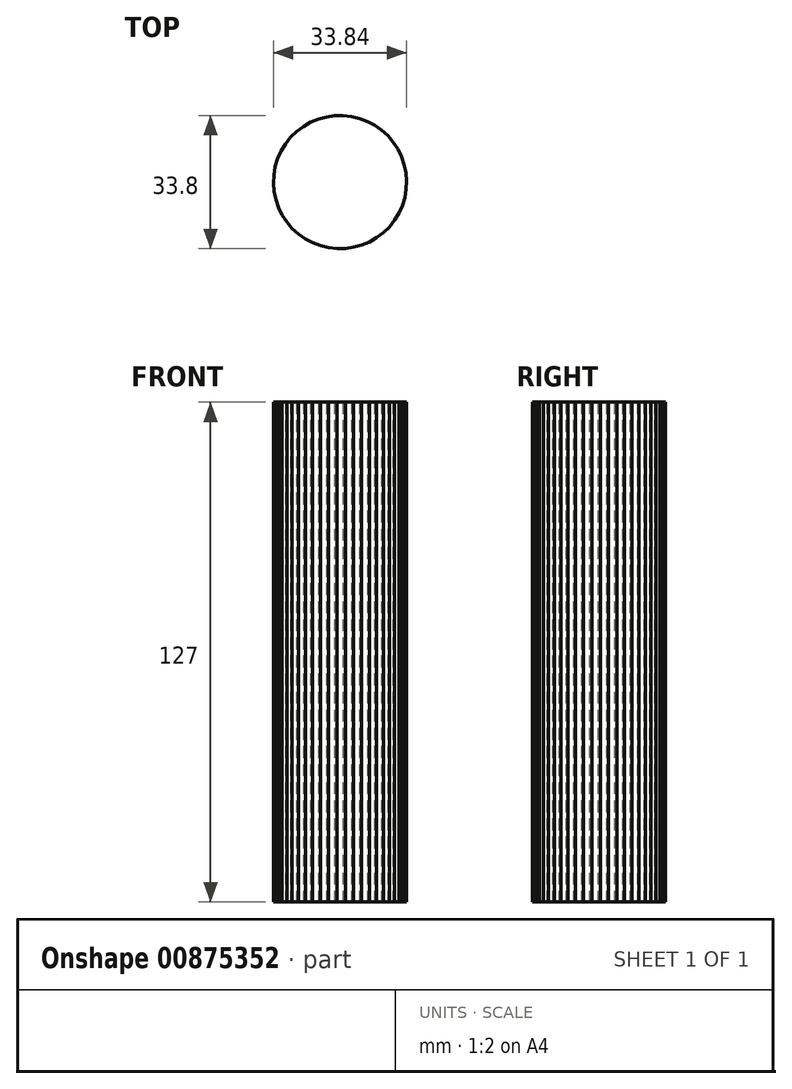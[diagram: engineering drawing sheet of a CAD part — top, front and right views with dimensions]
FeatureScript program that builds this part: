
annotation { "Feature Type Name" : "Feature", "Feature Type Description" : "" }
export const myFeature = defineFeature(function(context is Context, id is Id, definition is map)
    precondition{}
    {
        {
            var Q0;
            Q0=qCreatedBy(makeId("Top.planeOp"),FACE);
            var sketch = newSketch(context, id + "F0", { "sketchPlane" : qUnion([Q0])});
            skCircle(sketch, "E0.cCircle", {"center": v(-26.2, 25.5) * mm, "radius": 16.89 * mm, "construction": true});
            skLineSegment(sketch, "E0.0", {"start": v(-20.7, 9.5) * mm, "end": v(-22.75, 8.93) * mm});
            skLineSegment(sketch, "E0.1", {"start": v(-22.75, 8.93) * mm, "end": v(-24.85, 8.63) * mm});
            skLineSegment(sketch, "E0.2", {"start": v(-24.85, 8.63) * mm, "end": v(-26.97, 8.59) * mm});
            skLineSegment(sketch, "E0.3", {"start": v(-26.97, 8.59) * mm, "end": v(-29.09, 8.82) * mm});
            skLineSegment(sketch, "E0.4", {"start": v(-29.09, 8.82) * mm, "end": v(-31.15, 9.31) * mm});
            skLineSegment(sketch, "E0.5", {"start": v(-31.15, 9.31) * mm, "end": v(-33.14, 10.06) * mm});
            skLineSegment(sketch, "E0.6", {"start": v(-33.14, 10.06) * mm, "end": v(-35.02, 11.05) * mm});
            skLineSegment(sketch, "E0.7", {"start": v(-35.02, 11.05) * mm, "end": v(-36.76, 12.27) * mm});
            skLineSegment(sketch, "E0.8", {"start": v(-36.76, 12.27) * mm, "end": v(-38.33, 13.7) * mm});
            skLineSegment(sketch, "E0.9", {"start": v(-38.33, 13.7) * mm, "end": v(-39.72, 15.31) * mm});
            skLineSegment(sketch, "E0.10", {"start": v(-39.72, 15.31) * mm, "end": v(-40.88, 17.09) * mm});
            skLineSegment(sketch, "E0.11", {"start": v(-40.88, 17.09) * mm, "end": v(-41.82, 19) * mm});
            skLineSegment(sketch, "E0.12", {"start": v(-41.82, 19) * mm, "end": v(-42.51, 21) * mm});
            skLineSegment(sketch, "E0.13", {"start": v(-42.51, 21) * mm, "end": v(-42.95, 23.08) * mm});
            skLineSegment(sketch, "E0.14", {"start": v(-42.95, 23.08) * mm, "end": v(-43.12, 25.2) * mm});
            skLineSegment(sketch, "E0.15", {"start": v(-43.12, 25.2) * mm, "end": v(-43.02, 27.32) * mm});
            skLineSegment(sketch, "E0.16", {"start": v(-43.02, 27.32) * mm, "end": v(-42.66, 29.42) * mm});
            skLineSegment(sketch, "E0.17", {"start": v(-42.66, 29.42) * mm, "end": v(-42.03, 31.45) * mm});
            skLineSegment(sketch, "E0.18", {"start": v(-42.03, 31.45) * mm, "end": v(-41.16, 33.39) * mm});
            skLineSegment(sketch, "E0.19", {"start": v(-41.16, 33.39) * mm, "end": v(-40.05, 35.2) * mm});
            skLineSegment(sketch, "E0.20", {"start": v(-40.05, 35.2) * mm, "end": v(-38.73, 36.86) * mm});
            skLineSegment(sketch, "E0.21", {"start": v(-38.73, 36.86) * mm, "end": v(-37.2, 38.34) * mm});
            skLineSegment(sketch, "E0.22", {"start": v(-37.2, 38.34) * mm, "end": v(-35.5, 39.62) * mm});
            skLineSegment(sketch, "E0.23", {"start": v(-35.5, 39.62) * mm, "end": v(-33.66, 40.67) * mm});
            skLineSegment(sketch, "E0.24", {"start": v(-33.66, 40.67) * mm, "end": v(-31.7, 41.49) * mm});
            skLineSegment(sketch, "E0.25", {"start": v(-31.7, 41.49) * mm, "end": v(-29.65, 42.05) * mm});
            skLineSegment(sketch, "E0.26", {"start": v(-29.65, 42.05) * mm, "end": v(-27.55, 42.36) * mm});
            skLineSegment(sketch, "E0.27", {"start": v(-27.55, 42.36) * mm, "end": v(-25.43, 42.4) * mm});
            skLineSegment(sketch, "E0.28", {"start": v(-25.43, 42.4) * mm, "end": v(-23.31, 42.16) * mm});
            skLineSegment(sketch, "E0.29", {"start": v(-23.31, 42.16) * mm, "end": v(-21.25, 41.67) * mm});
            skLineSegment(sketch, "E0.30", {"start": v(-21.25, 41.67) * mm, "end": v(-19.26, 40.92) * mm});
            skLineSegment(sketch, "E0.31", {"start": v(-19.26, 40.92) * mm, "end": v(-17.38, 39.93) * mm});
            skLineSegment(sketch, "E0.32", {"start": v(-17.38, 39.93) * mm, "end": v(-15.64, 38.7) * mm});
            skLineSegment(sketch, "E0.33", {"start": v(-15.64, 38.7) * mm, "end": v(-14.07, 37.28) * mm});
            skLineSegment(sketch, "E0.34", {"start": v(-14.07, 37.28) * mm, "end": v(-12.68, 35.67) * mm});
            skLineSegment(sketch, "E0.35", {"start": v(-12.68, 35.67) * mm, "end": v(-11.52, 33.9) * mm});
            skLineSegment(sketch, "E0.36", {"start": v(-11.52, 33.9) * mm, "end": v(-10.58, 31.99) * mm});
            skLineSegment(sketch, "E0.37", {"start": v(-10.58, 31.99) * mm, "end": v(-9.89, 29.98) * mm});
            skLineSegment(sketch, "E0.38", {"start": v(-9.89, 29.98) * mm, "end": v(-9.45, 27.9) * mm});
            skLineSegment(sketch, "E0.39", {"start": v(-9.45, 27.9) * mm, "end": v(-9.28, 25.78) * mm});
            skLineSegment(sketch, "E0.40", {"start": v(-9.28, 25.78) * mm, "end": v(-9.38, 23.66) * mm});
            skLineSegment(sketch, "E0.41", {"start": v(-9.38, 23.66) * mm, "end": v(-9.74, 21.56) * mm});
            skLineSegment(sketch, "E0.42", {"start": v(-9.74, 21.56) * mm, "end": v(-10.37, 19.53) * mm});
            skLineSegment(sketch, "E0.43", {"start": v(-10.37, 19.53) * mm, "end": v(-11.24, 17.6) * mm});
            skLineSegment(sketch, "E0.44", {"start": v(-11.24, 17.6) * mm, "end": v(-12.35, 15.78) * mm});
            skLineSegment(sketch, "E0.45", {"start": v(-12.35, 15.78) * mm, "end": v(-13.67, 14.12) * mm});
            skLineSegment(sketch, "E0.46", {"start": v(-13.67, 14.12) * mm, "end": v(-15.2, 12.64) * mm});
            skLineSegment(sketch, "E0.47", {"start": v(-15.2, 12.64) * mm, "end": v(-16.9, 11.36) * mm});
            skLineSegment(sketch, "E0.48", {"start": v(-16.9, 11.36) * mm, "end": v(-18.74, 10.3) * mm});
            skLineSegment(sketch, "E0.49", {"start": v(-18.74, 10.3) * mm, "end": v(-20.7, 9.5) * mm});
            skPoint(sketch, "E0.0.midPoint", {"position": v(-21.72, 9.2) * mm});
            skSolve(sketch);
        }
        {
            var Q0;
            Q0 = qSketchRegion(id + "F0", true);
            extrude(context, id + "F1", {"entities" : qUnion([Q0]), "depth" : 127 * mm, "offsetDistance" : 25.4 * mm});
        }
    });
